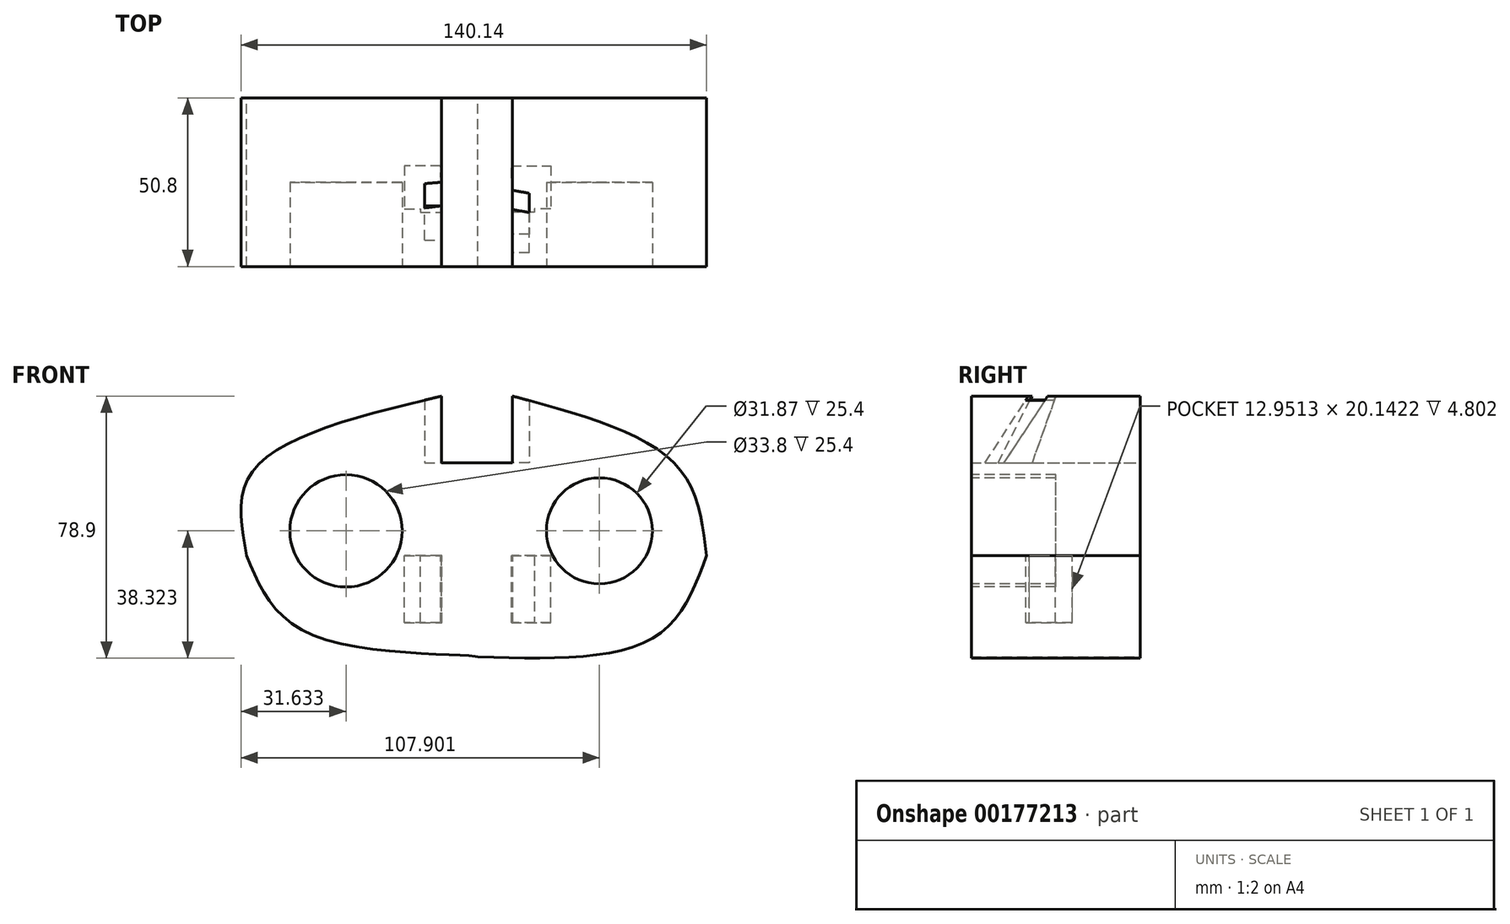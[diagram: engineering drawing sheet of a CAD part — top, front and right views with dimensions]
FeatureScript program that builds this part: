
annotation { "Feature Type Name" : "Feature", "Feature Type Description" : "" }
export const myFeature = defineFeature(function(context is Context, id is Id, definition is map)
    precondition{}
    {
        {
            var Q0;
            Q0=qCreatedBy(makeId("Front.planeOp"),FACE);
            var sketch = newSketch(context, id + "F0", { "sketchPlane" : qUnion([Q0])});
            skLineSegment(sketch, "E0", {"start": v(-10.94, 27.92) * mm, "end": v(10.36, 27.92) * mm});
            skLineSegment(sketch, "E1", {"start": v(10.36, 27.92) * mm, "end": v(10.36, 48.06) * mm});
            skLineSegment(sketch, "E2", {"start": v(-10.94, 27.92) * mm, "end": v(-10.94, 48.06) * mm});
            skFitSpline(sketch, "E3", {"points": [v(-69.65, 0) * mm, v(-67.92, 25.33) * mm, v(-10.94, 48.06) * mm], "startDerivative": vector(-13.05, 70.05) * mm, "endDerivative": vector(120.8, 29.04) * mm});
            skFitSpline(sketch, "E4", {"points": [v(10.36, 48.06) * mm, v(59.58, 27.34) * mm, v(68.79, 0) * mm], "startDerivative": vector(103.73, -27.72) * mm, "endDerivative": vector(8.26, -70.6) * mm});
            skFitSpline(sketch, "E5", {"points": [v(-69.65, 0) * mm, v(-48.35, -24.46) * mm, v(0, -30.5) * mm, v(0, -30.8) * mm], "startDerivative": vector(27.62, -67.9) * mm, "endDerivative": vector(-4.22, -7.42) * mm});
            skFitSpline(sketch, "E6", {"points": [v(0, -30.5) * mm, v(53.24, -24.46) * mm, v(68.79, 0) * mm], "startDerivative": vector(108.46, -3.12) * mm, "endDerivative": vector(24.87, 67.74) * mm});
            skSolve(sketch);
        }
        {
            var Q0;
            Q0 = qSketchRegion(id + "F0", true);
            extrude(context, id + "F1", {"entities" : qUnion([Q0]), "depth" : 50.8 * mm});
        }
        {
            var Q0;
            Q0=makeQuery(id+"F1.opExtrude","CAP_FACE",FACE,{"disambiguationData":[OSD([sQuery(id+"F0.wireOp",EDGE,"E0"),sQuery(id+"F0.wireOp",EDGE,"E1"),sQuery(id+"F0.wireOp",EDGE,"E2"),sQuery(id+"F0.wireOp",EDGE,"E3"),sQuery(id+"F0.wireOp",EDGE,"E4"),sQuery(id+"F0.wireOp",EDGE,"E5"),sQuery(id+"F0.wireOp",EDGE,"E6")])],"isStart":false});
            var sketch = newSketch(context, id + "F2", { "sketchPlane" : qUnion([Q0])});
            skCircle(sketch, "E7", {"center": v(-39.72, 7.48) * mm, "radius": 16.9 * mm});
            skCircle(sketch, "E8", {"center": v(36.55, 7.48) * mm, "radius": 15.93 * mm});
            skSolve(sketch);
        }
        {
            var Q0;
            Q0 = qSketchRegion(id + "F2", true);
            extrude(context, id + "F3", {"entities" : qUnion([Q0]), "operationType" : NewBodyOperationType.REMOVE, "oppositeDirection" : true, "depth" : 25.4 * mm});
        }
        {
            var Q0;
            Q0=qCreatedBy(makeId("Top.planeOp"),FACE);
            var sketch = newSketch(context, id + "F4", { "sketchPlane" : qUnion([Q0])});
            skLineSegment(sketch, "E9", {"start": v(-10.9, -25.49) * mm, "end": v(-17.36, -25.49) * mm});
            skLineSegment(sketch, "E10", {"start": v(-17.36, -25.49) * mm, "end": v(-17.36, -34.44) * mm});
            skLineSegment(sketch, "E11", {"start": v(-17.36, -34.44) * mm, "end": v(-10.9, -34.44) * mm});
            skLineSegment(sketch, "E12", {"start": v(-10.9, -34.44) * mm, "end": v(-10.9, -25.49) * mm});
            skLineSegment(sketch, "E13", {"start": v(10.35, -25.49) * mm, "end": v(17.02, -25.49) * mm});
            skLineSegment(sketch, "E14", {"start": v(17.02, -25.49) * mm, "end": v(17.02, -34.44) * mm});
            skLineSegment(sketch, "E15", {"start": v(17.02, -34.44) * mm, "end": v(10.48, -34.44) * mm});
            skLineSegment(sketch, "E16", {"start": v(10.48, -34.44) * mm, "end": v(10.35, -25.49) * mm});
            skSolve(sketch);
        }
        {
            var Q0;
            Q0 = qSketchRegion(id + "F4", true);
            extrude(context, id + "F5", {"entities" : qUnion([Q0]), "operationType" : NewBodyOperationType.REMOVE, "oppositeDirection" : true, "depth" : 20.14 * mm});
        }
        {
            var Q0;
            Q0=qCreatedBy(makeId("Top.planeOp"),FACE);
            var sketch = newSketch(context, id + "F6", { "sketchPlane" : qUnion([Q0])});
            skLineSegment(sketch, "E17", {"start": v(-11.22, -20.43) * mm, "end": v(-22.16, -20.43) * mm});
            skLineSegment(sketch, "E18", {"start": v(-22.16, -20.43) * mm, "end": v(-22.16, -33.39) * mm});
            skLineSegment(sketch, "E19", {"start": v(-22.16, -33.39) * mm, "end": v(-10.94, -33.39) * mm});
            skLineSegment(sketch, "E20", {"start": v(-10.94, -33.39) * mm, "end": v(-11.22, -20.43) * mm});
            skLineSegment(sketch, "E21", {"start": v(10.07, -20.43) * mm, "end": v(21.87, -20.43) * mm});
            skLineSegment(sketch, "E22", {"start": v(21.87, -20.43) * mm, "end": v(21.87, -33.39) * mm});
            skLineSegment(sketch, "E23", {"start": v(21.87, -33.39) * mm, "end": v(10.36, -33.39) * mm});
            skLineSegment(sketch, "E24", {"start": v(10.36, -33.39) * mm, "end": v(10.07, -20.43) * mm});
            skSolve(sketch);
        }
        {
            var Q0;
            Q0 = qSketchRegion(id + "F6", true);
            extrude(context, id + "F7", {"entities" : qUnion([Q0]), "operationType" : NewBodyOperationType.REMOVE, "oppositeDirection" : true, "depth" : 20.14 * mm});
        }
        {
            var Q0;
            Q0=makeQuery(id+"F1.opExtrude","SWEPT_FACE",FACE,{"disambiguationData":[OSD([sQuery(id+"F0.wireOp",EDGE,"E2")])]});
            var sketch = newSketch(context, id + "F8", { "sketchPlane" : qUnion([Q0])});
            skLineSegment(sketch, "E25", {"start": v(-25.4, 48.06) * mm, "end": v(-32.53, 27.92) * mm});
            skLineSegment(sketch, "E26", {"start": v(-32.53, 27.92) * mm, "end": v(-42.79, 27.92) * mm});
            skLineSegment(sketch, "E27", {"start": v(-42.79, 27.92) * mm, "end": v(-32.53, 48.06) * mm});
            skLineSegment(sketch, "E28", {"start": v(-32.53, 48.06) * mm, "end": v(-25.4, 48.06) * mm});
            skSolve(sketch);
        }
        {
            var Q0;
            Q0 = qSketchRegion(id + "F8", true);
            extrude(context, id + "F9", {"entities" : qUnion([Q0]), "operationType" : NewBodyOperationType.REMOVE, "oppositeDirection" : true, "depth" : 5.08 * mm});
        }
        {
            var Q0;
            Q0=qCreatedBy(makeId("Front.planeOp"),FACE);
            var sketch = newSketch(context, id + "F10", { "sketchPlane" : qUnion([Q0])});
            skLineSegment(sketch, "E29", {"start": v(20.95, 46.18) * mm, "end": v(29.16, 24.87) * mm});
            skLineSegment(sketch, "E30", {"start": v(29.16, 24.87) * mm, "end": v(35.55, 23.4) * mm});
            skLineSegment(sketch, "E31", {"start": v(35.55, 23.4) * mm, "end": v(29.16, 44.91) * mm});
            skLineSegment(sketch, "E32", {"start": v(29.16, 44.91) * mm, "end": v(20.95, 46.18) * mm});
            skSolve(sketch);
        }
        {
            var Q0;
            Q0 = qSketchRegion(id + "F10", true);
            extrude(context, id + "F11", {"entities" : qUnion([Q0]), "operationType" : NewBodyOperationType.REMOVE, "oppositeDirection" : true, "depth" : 5.08 * mm});
        }
        {
            var Q0;
            Q0=makeQuery(id+"F1.opExtrude","SWEPT_FACE",FACE,{"disambiguationData":[OSD([sQuery(id+"F0.wireOp",EDGE,"E1")])]});
            var sketch = newSketch(context, id + "F12", { "sketchPlane" : qUnion([Q0])});
            skLineSegment(sketch, "E33", {"start": v(27.84, 48.06) * mm, "end": v(41.08, 27.92) * mm});
            skLineSegment(sketch, "E34", {"start": v(41.08, 27.92) * mm, "end": v(46.7, 27.92) * mm});
            skLineSegment(sketch, "E35", {"start": v(46.7, 27.92) * mm, "end": v(33.64, 48.06) * mm});
            skLineSegment(sketch, "E36", {"start": v(33.64, 48.06) * mm, "end": v(27.84, 48.06) * mm});
            skSolve(sketch);
        }
        {
            var Q0;
            Q0 = qSketchRegion(id + "F12", true);
            extrude(context, id + "F13", {"entities" : qUnion([Q0]), "operationType" : NewBodyOperationType.REMOVE, "oppositeDirection" : true, "depth" : 5.08 * mm});
        }
    });
